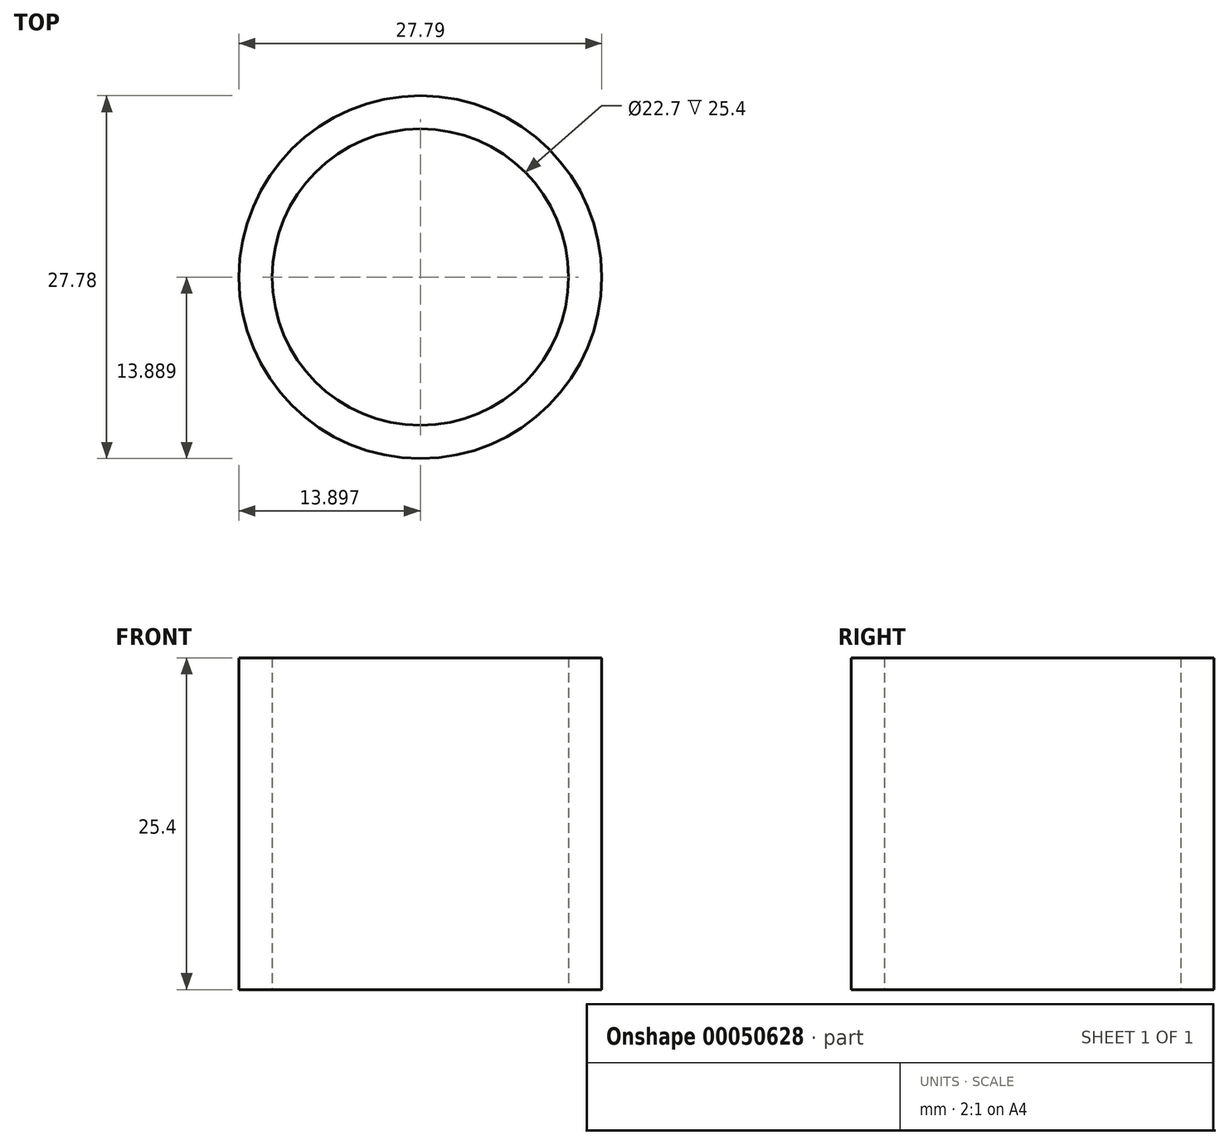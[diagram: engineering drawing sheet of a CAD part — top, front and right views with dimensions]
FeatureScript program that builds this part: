
annotation { "Feature Type Name" : "Feature", "Feature Type Description" : "" }
export const myFeature = defineFeature(function(context is Context, id is Id, definition is map)
    precondition{}
    {
        {
            var Q0;
            Q0=qCreatedBy(makeId("Top.planeOp"),FACE);
            var sketch = newSketch(context, id + "F0", { "sketchPlane" : qUnion([Q0])});
            skCircle(sketch, "E0", {"center": v(-55.06, 14.09) * mm, "radius": 13.9 * mm});
            skCircle(sketch, "E1", {"center": v(-55.06, 14.09) * mm, "radius": 11.35 * mm});
            skSolve(sketch);
        }
        {
            var Q0;
            Q0=makeQuery(id+"F0.imprint","IMPRINT",FACE,{"disambiguationData":[TD([[makeQuery(id+"F0.imprint","IMPRINT",EDGE,{"derivedFrom":sQuery(id+"F0.wireOp",EDGE,"E1")}),1.0]])]});
            var sketch = newSketch(context, id + "F1", { "sketchPlane" : qUnion([Q0])});
            skSolve(sketch);
        }
        {
            var Q0;
            Q0=makeQuery(id+"F1.imprint","IMPRINT",FACE,{"disambiguationData":[TD([[makeQuery(id+"F1.imprint","IMPRINT",EDGE,{"derivedFrom":makeQuery(id+"F0.imprint","IMPRINT",EDGE,{"derivedFrom":sQuery(id+"F0.wireOp",EDGE,"E1")})}),1.0]])]});
            var sketch = newSketch(context, id + "F2", { "sketchPlane" : qUnion([Q0])});
            skSolve(sketch);
        }
        {
            var Q0;
            Q0=makeQuery(id+"F2.imprint","IMPRINT",FACE,{"disambiguationData":[TD([[makeQuery(id+"F2.imprint","IMPRINT",EDGE,{"derivedFrom":makeQuery(id+"F1.imprint","IMPRINT",EDGE,{"derivedFrom":makeQuery(id+"F0.imprint","IMPRINT",EDGE,{"derivedFrom":sQuery(id+"F0.wireOp",EDGE,"E1")})})}),1.0]])]});
            var sketch = newSketch(context, id + "F3", { "sketchPlane" : qUnion([Q0])});
            skSolve(sketch);
        }
        {
            var Q0;
            Q0=makeQuery(id+"F3.imprint","IMPRINT",FACE,{"disambiguationData":[TD([[makeQuery(id+"F3.imprint","IMPRINT",EDGE,{"derivedFrom":makeQuery(id+"F2.imprint","IMPRINT",EDGE,{"derivedFrom":makeQuery(id+"F1.imprint","IMPRINT",EDGE,{"derivedFrom":makeQuery(id+"F0.imprint","IMPRINT",EDGE,{"derivedFrom":sQuery(id+"F0.wireOp",EDGE,"E1")})})})}),1.0]])]});
            var Q1;
            Q1=makeQuery(id+"F0.imprint","IMPRINT",FACE,{"disambiguationData":[TD([[makeQuery(id+"F0.imprint","IMPRINT",EDGE,{"derivedFrom":sQuery(id+"F0.wireOp",EDGE,"E0")}),1.0]])]});
            extrude(context, id + "F4", {"entities" : qUnion([Q0, Q1]), "depth" : 25.4 * mm});
        }
        {
            var Q0;
            Q0=makeQuery(id+"F4.opExtrude","CAP_FACE",FACE,{"disambiguationData":[OSD([sQuery(id+"F0.wireOp",EDGE,"E1")])],"isStart":false});
            var sketch = newSketch(context, id + "F5", { "sketchPlane" : qUnion([Q0])});
            skSolve(sketch);
        }
        {
            var Q0;
            {var subQ0=sQuery(id+"F0.wireOp",EDGE,"E1");Q0=makeQuery(id+"F5.imprint","IMPRINT",FACE,{"disambiguationData":[TD([[makeQuery(id+"F5.imprint","IMPRINT",EDGE,{"derivedFrom":makeQuery(id+"F4.opExtrude","CAP_EDGE",EDGE,{"disambiguationData":[OSD([subQ0]),TDD([makeQuery(id+"F3.imprint","IMPRINT",EDGE,{"derivedFrom":makeQuery(id+"F2.imprint","IMPRINT",EDGE,{"derivedFrom":makeQuery(id+"F1.imprint","IMPRINT",EDGE,{"derivedFrom":makeQuery(id+"F0.imprint","IMPRINT",EDGE,{"derivedFrom":subQ0})})})})])],"isStart":false})}),1.0]])]});}
            extrude(context, id + "F6", {"entities" : qUnion([Q0]), "operationType" : NewBodyOperationType.REMOVE, "endBound" : BoundingType.THROUGH_ALL, "oppositeDirection" : true, "depth" : 25.4 * mm});
        }
    });
